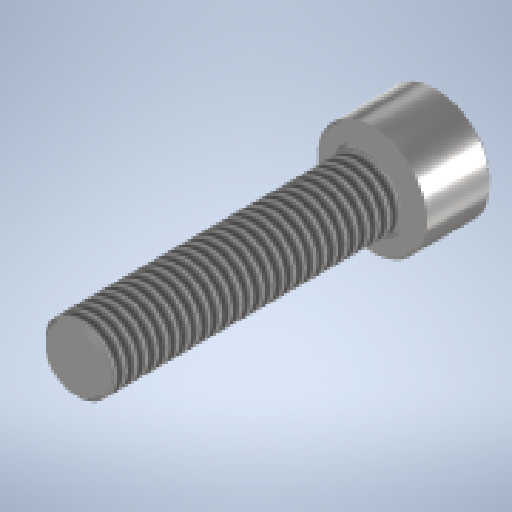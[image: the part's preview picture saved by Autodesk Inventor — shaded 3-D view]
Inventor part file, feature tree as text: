
AUTODESK INVENTOR PART (.ipt)
format: ipt  version: 2024 (Build 280153000, 153)  size: 193,536 bytes
history: native  units: mm
features: extrude x3, chamfer x3, sketch x2, thread x1, hole x1
ambient origin geometry x8: Origin, YZ Plane, XZ Plane, XY Plane, X Axis, Y Axis, Z Axis, Center Point
bodies: Solid1 (feature_tree)
feature tree (10):
  sketch  "Sketch1"  dims[d0=13.0mm d1=8.0mm]
  extrude  "Extrusion1"  Depth=8.0mm
  extrude  "Extrusion2"  Depth=4.0mm TaperAngle=0.0deg
  thread  "Thread1"  [1 undecoded]
  chamfer  "Chamfer1"  Distance=6.0mm
  sketch  "Sketch2"  dims[d2=35.0mm d3=0.0mm d4=8.0mm d5=0.0mm d6=25.0mm d7=0.0mm d8=0.25mm d9=2.0mm d10=45.0deg d11=5.5mm d12=6.0mm d15=1.0mm d16=2.0mm d17=45.0deg d18=3.0mm d19=0.0mm d20=0.5mm d21=2.0mm d22=45.0deg d23=5.5mm d24=6.0mm d25=4.0mm d26=2.0mm d27=90.0deg d28=4.0mm d29=150.0deg]
  hole  "Hole1"  [1 undecoded]
  chamfer  "Chamfer2"  Distance=3.0mm
  extrude  "Extrusion4"  Depth=4.0mm TaperAngle=45.0deg
  chamfer  "Chamfer3"  Distance=5.5mm
note: 2 required parameter values undecoded (feature->parameter linkage not recoverable at this tier; creation-order binding heuristic only, values carry confidence <= 0.55)
